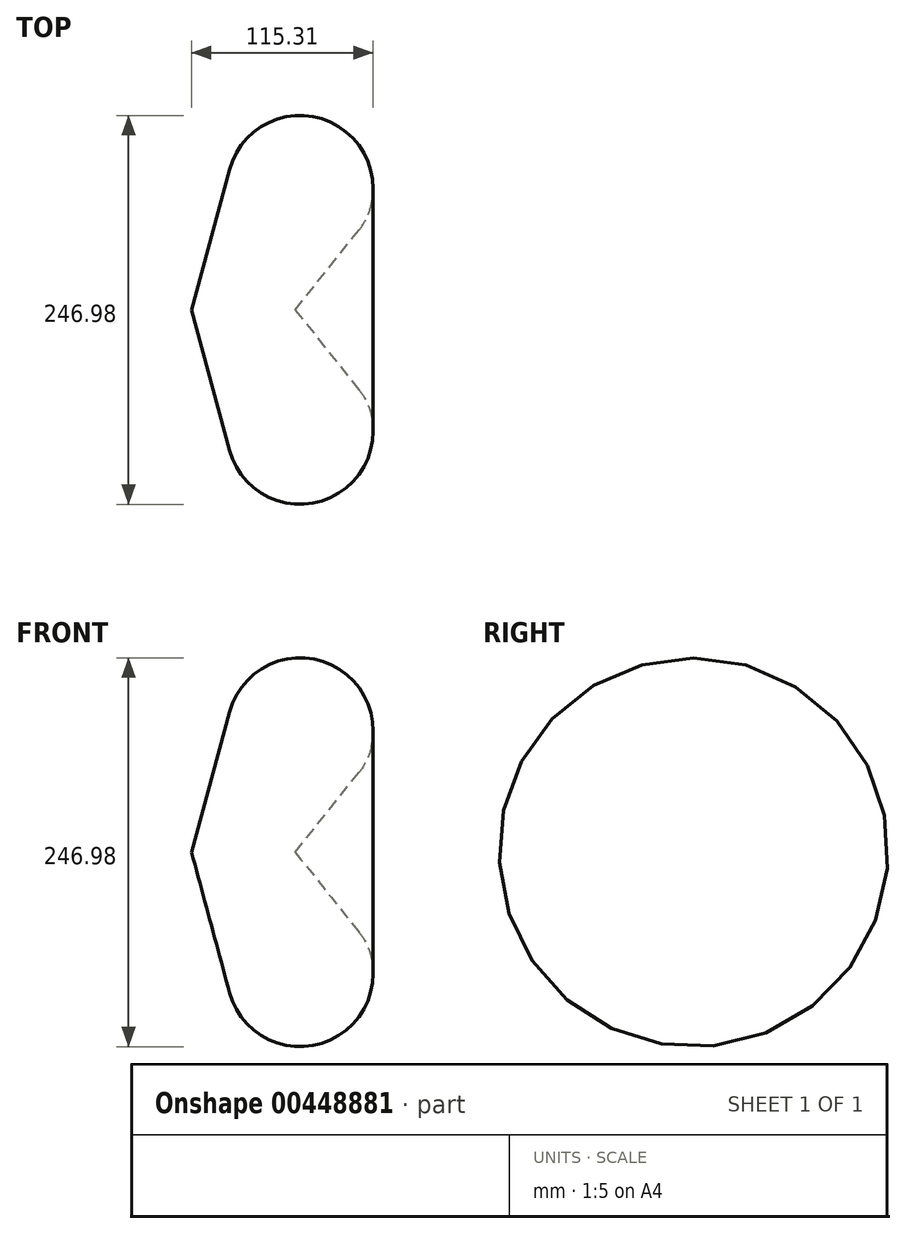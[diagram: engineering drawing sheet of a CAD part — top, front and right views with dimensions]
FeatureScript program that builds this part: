
annotation { "Feature Type Name" : "Feature", "Feature Type Description" : "" }
export const myFeature = defineFeature(function(context is Context, id is Id, definition is map)
    precondition{}
    {
        {
            var Q0;
            Q0=qCreatedBy(makeId("Front.planeOp"),FACE);
            var sketch = newSketch(context, id + "F0", { "sketchPlane" : qUnion([Q0])});
            skLineSegment(sketch, "E0", {"start": v(24.17, 54.85) * mm, "end": v(0, -34.38) * mm});
            skLineSegment(sketch, "E1", {"start": v(0, -34.38) * mm, "end": v(65.83, -34.38) * mm});
            skArc(sketch, "E2", {"start": v(24.17, 54.85) * mm, "mid": v(86.33, 85.73) * mm, "end": v(109.54, 20.32) * mm});
            skLineSegment(sketch, "E3", {"start": v(68.93, 42.73) * mm, "end": v(68.93, 42.73) * mm});
            skLineSegment(sketch, "E4", {"start": v(65.83, -34.38) * mm, "end": v(109.54, 20.32) * mm});
            skSolve(sketch);
        }
        {
            var Q0;
            Q0=makeQuery(id+"F0.imprint","IMPRINT",FACE,{"disambiguationData":[TD([[makeQuery(id+"F0.imprint","IMPRINT",EDGE,{"derivedFrom":sQuery(id+"F0.wireOp",EDGE,"E0")}),1.0]])]});
            var Q1;
            Q1 = qSketchRegion(id + "F0", true);
            var Q2;
            Q2=sQuery(id+"F0.wireOp",EDGE,"E1");
            revolve(context, id + "F1", {"bodyType" : ToolBodyType.SURFACE, "entities" : qUnion([Q0]), "surfaceEntities" : qUnion([Q1]), "axis" : qUnion([Q2]), "revolveType" : RevolveType.FULL});
        }
        {
            var Q0;
            Q0=makeQuery(id+"F1.opRevolve","SWEPT_EDGE",EDGE,{"disambiguationData":[OSD([sQuery(id+"F0.wireOp",EDGE,"E2"),sQuery(id+"F0.wireOp",EDGE,"E4")])]});
            fillet(context, id + "F2", {"entities" : qUnion([Q0]), "radius" : 40 * mm, "tangentPropagation" : true, "allowEdgeOverflow" : false});
        }
    });
